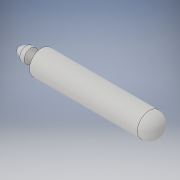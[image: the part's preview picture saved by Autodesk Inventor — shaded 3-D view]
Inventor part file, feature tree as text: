
AUTODESK INVENTOR PART (.ipt)
format: ipt  version: 2018.3 (Build 223284000, 284)  size: 127,488 bytes
history: native  units: in
note: dims shown in document units (in); Inventor stores cm internally (conversion verified against a paired STEP export)
features: revolve x1, sketch x1
ambient origin geometry x8: Origin, YZ Plane, XZ Plane, XY Plane, X Axis, Y Axis, Z Axis, Center Point
bodies: Solid1 (feature_tree)
feature tree (2):
  revolve  "Revolution1"  Angle=30.0deg
  sketch  "Sketch1"  dims[d0=0.0125in d1=30.0deg d2=0.0323in d3=0.62in d4=0.0575in d6=0.054in d7=90.0deg]
